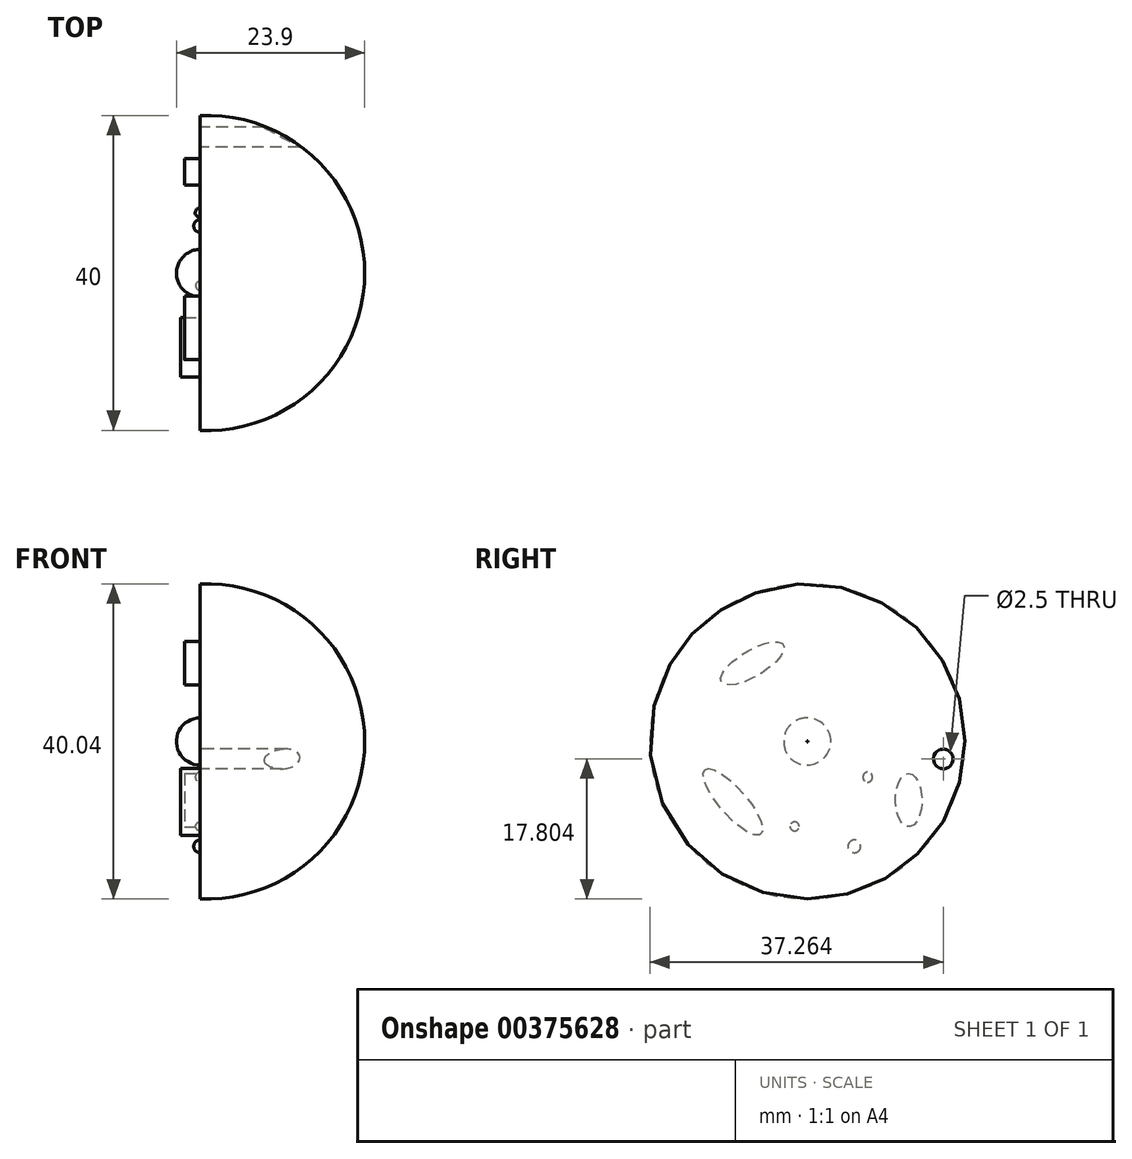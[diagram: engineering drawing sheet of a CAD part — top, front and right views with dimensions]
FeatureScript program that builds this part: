
annotation { "Feature Type Name" : "Feature", "Feature Type Description" : "" }
export const myFeature = defineFeature(function(context is Context, id is Id, definition is map)
    precondition{}
    {
        {
            var Q0;
            Q0=qCreatedBy(makeId("Front.planeOp"),FACE);
            var sketch = newSketch(context, id + "F0", { "sketchPlane" : qUnion([Q0])});
            skLineSegment(sketch, "E0", {"start": v(0, 0) * mm, "end": v(0, 20) * mm});
            skLineSegment(sketch, "E1", {"start": v(0, 0) * mm, "end": v(20.9, 0) * mm});
            skArc(sketch, "E2", {"start": v(20.9, 0) * mm, "mid": v(14.71, 14.46) * mm, "end": v(0, 20) * mm});
            skSolve(sketch);
        }
        {
            var Q0;
            Q0=makeQuery(id+"F0.imprint","IMPRINT",FACE,{"disambiguationData":[TD([[makeQuery(id+"F0.imprint","IMPRINT",EDGE,{"derivedFrom":sQuery(id+"F0.wireOp",EDGE,"E0")}),-1.0]])]});
            var Q1;
            Q1=sQuery(id+"F0.wireOp",EDGE,"E1");
            revolve(context, id + "F1", {"entities" : qUnion([Q0]), "axis" : qUnion([Q1]), "revolveType" : RevolveType.FULL});
        }
        {
            var Q0;
            Q0=qCreatedBy(makeId("Right.planeOp"),FACE);
            var sketch = newSketch(context, id + "F2", { "sketchPlane" : qUnion([Q0])});
            skLineSegment(sketch, "E3", {"start": v(0, 0) * mm, "end": v(0, 3) * mm});
            skLineSegment(sketch, "E4", {"start": v(0, 0) * mm, "end": v(-3, 0) * mm});
            skArc(sketch, "E5", {"start": v(0, 3) * mm, "mid": v(-2.14, 2.14) * mm, "end": v(-3, 0) * mm});
            skSolve(sketch);
        }
        {
            var Q0;
            Q0=qSketchRegion(id+"F2",true);
            var Q1;
            Q1=sQuery(id+"F2.wireOp",EDGE,"E4");
            revolve(context, id + "F3", {"operationType" : NewBodyOperationType.ADD, "entities" : qUnion([Q0]), "axis" : qUnion([Q1]), "revolveType" : RevolveType.FULL});
        }
        {
            var Q0;
            Q0=makeQuery(id+"F1.opRevolve","SWEPT_FACE",FACE,{"disambiguationData":[OSD([sQuery(id+"F0.wireOp",EDGE,"E0")])]});
            var sketch = newSketch(context, id + "F4", { "sketchPlane" : qUnion([Q0])});
            skLineSegment(sketch, "E6", {"start": v(0, 0) * mm, "end": v(-3, 0) * mm});
            skLineSegment(sketch, "E7", {"start": v(0, 0) * mm, "end": v(0, 3) * mm});
            skArc(sketch, "E8", {"start": v(0, 3) * mm, "mid": v(-2.1, 2.1) * mm, "end": v(-3, 0) * mm});
            skSolve(sketch);
        }
        {
            var Q0;
            Q0=makeQuery(id+"F4.imprint","IMPRINT",FACE,{"disambiguationData":[TD([[makeQuery(id+"F4.imprint","IMPRINT",EDGE,{"derivedFrom":sQuery(id+"F4.wireOp",EDGE,"E6")}),-1.0]])]});
            var Q1;
            Q1=sQuery(id+"F4.wireOp",EDGE,"E6");
            revolve(context, id + "F5", {"operationType" : NewBodyOperationType.ADD, "entities" : qUnion([Q0]), "axis" : qUnion([Q1]), "revolveType" : RevolveType.FULL});
        }
        {
            var Q0;
            Q0=makeQuery(id+"F1.opRevolve","SWEPT_FACE",FACE,{"disambiguationData":[OSD([sQuery(id+"F0.wireOp",EDGE,"E0")])]});
            var sketch = newSketch(context, id + "F6", { "sketchPlane" : qUnion([Q0])});
            skEllipse(sketch, "E9", {"center": v(9.46, -7.67) * mm, "majorRadius": 5.42 * mm, "minorRadius": 1.7 * mm, "majorAxis": v(0.66, 0.75)});
            skSolve(sketch);
        }
        {
            var Q0;
            Q0=qSketchRegion(id+"F6",true);
            extrude(context, id + "F7", {"entities" : qUnion([Q0]), "depth" : 2.5 * mm});
        }
        {
            var Q0;
            Q0=makeQuery(id+"F7.opExtrude","CAP_FACE",FACE,{"disambiguationData":[OSD([sQuery(id+"F6.wireOp",EDGE,"E9")])],"isStart":false});
            var sketch = newSketch(context, id + "F8", { "sketchPlane" : qUnion([Q0])});
            skFitSpline(sketch, "E10", {"points": [v(7.97, -11.28) * mm, v(6.8, -8.9) * mm, v(9.38, -10.19) * mm, v(8.17, -7.24) * mm, v(11, -8.49) * mm, v(9.27, -5.4) * mm, v(11.92, -6.7) * mm, v(11.05, -4) * mm, v(13.1, -5.01) * mm], "startDerivative": vector(-20.7, 30.85) * mm, "endDerivative": vector(27.66, -19.9) * mm});
            skSolve(sketch);
        }
        {
            var Q0;
            Q0=qSketchRegion(id+"F8",true);
            var Q1;
            Q1=sQuery(id+"F8.wireOp",EDGE,"E10");
            extrude(context, id + "F9", {"entities" : qUnion([Q0]), "bodyType" : ToolBodyType.SURFACE, "surfaceEntities" : qUnion([Q1]), "oppositeDirection" : true, "depth" : 2 * mm});
        }
        {
            var Q0;
            Q0=makeQuery(id+"F1.opRevolve","SWEPT_FACE",FACE,{"disambiguationData":[OSD([sQuery(id+"F0.wireOp",EDGE,"E0")])]});
            var sketch = newSketch(context, id + "F10", { "sketchPlane" : qUnion([Q0])});
            skSolve(sketch);
        }
        {
            var Q0;
            {var subQ1=sQuery(id+"F0.wireOp",EDGE,"E0");Q0=makeQuery(id+"F10.imprint","IMPRINT",FACE,{"disambiguationData":[TD([[makeQuery(id+"F10.imprint","IMPRINT",EDGE,{"derivedFrom":makeQuery(id+"F1.opRevolve","SWEPT_EDGE",EDGE,{"disambiguationData":[OSD([subQ1,sQuery(id+"F0.wireOp",EDGE,"E2")])]})}),1.0]])]});}
            var sketch = newSketch(context, id + "F11", { "sketchPlane" : qUnion([Q0])});
            skSolve(sketch);
        }
        {
            var Q0;
            {var subQ1=sQuery(id+"F0.wireOp",EDGE,"E0");Q0=makeQuery(id+"F10.imprint","IMPRINT",FACE,{"disambiguationData":[TD([[makeQuery(id+"F10.imprint","IMPRINT",EDGE,{"derivedFrom":makeQuery(id+"F1.opRevolve","SWEPT_EDGE",EDGE,{"disambiguationData":[OSD([subQ1,sQuery(id+"F0.wireOp",EDGE,"E2")])]})}),1.0]])]});}
            var sketch = newSketch(context, id + "F12", { "sketchPlane" : qUnion([Q0])});
            skEllipse(sketch, "E11", {"center": v(6.98, 9.93) * mm, "majorRadius": 4.6 * mm, "minorRadius": 1.66 * mm, "majorAxis": v(0.86, -0.51)});
            skSolve(sketch);
        }
        {
            var Q0;
            Q0=qSketchRegion(id+"F12",true);
            extrude(context, id + "F13", {"entities" : qUnion([Q0]), "depth" : 2 * mm});
        }
        {
            var Q0;
            Q0=makeQuery(id+"F13.opExtrude","CAP_FACE",FACE,{"disambiguationData":[OSD([sQuery(id+"F12.wireOp",EDGE,"E11")])],"isStart":false});
            var sketch = newSketch(context, id + "F14", { "sketchPlane" : qUnion([Q0])});
            skFitSpline(sketch, "E12", {"points": [v(4.68, 12.63) * mm, v(3.63, 10.54) * mm, v(6.2, 12.18) * mm, v(5.11, 9.18) * mm, v(7.84, 11.35) * mm, v(6.92, 8.06) * mm, v(9.45, 10.2) * mm, v(9.08, 7.26) * mm], "startDerivative": vector(-17.32, -26.87) * mm, "endDerivative": vector(-10.03, -33.63) * mm});
            skSolve(sketch);
        }
        {
            var Q0;
            Q0=qSketchRegion(id+"F14",true);
            var Q1;
            Q1=sQuery(id+"F14.wireOp",EDGE,"E12");
            extrude(context, id + "F15", {"entities" : qUnion([Q0]), "bodyType" : ToolBodyType.SURFACE, "surfaceEntities" : qUnion([Q1]), "oppositeDirection" : true, "depth" : 2 * mm});
        }
        {
            var Q0;
            {var subQ1=sQuery(id+"F0.wireOp",EDGE,"E0");Q0=makeQuery(id+"F10.imprint","IMPRINT",FACE,{"disambiguationData":[TD([[makeQuery(id+"F10.imprint","IMPRINT",EDGE,{"derivedFrom":makeQuery(id+"F1.opRevolve","SWEPT_EDGE",EDGE,{"disambiguationData":[OSD([subQ1,sQuery(id+"F0.wireOp",EDGE,"E2")])]})}),1.0]])]});}
            var sketch = newSketch(context, id + "F16", { "sketchPlane" : qUnion([Q0])});
            skFitSpline(sketch, "E13", {"points": [v(-13.4, 3.83) * mm, v(-13, 6.76) * mm, v(-11.02, 11.05) * mm, v(-7.06, 13.56) * mm, v(-3.83, 13.87) * mm, v(-2.72, 12.84) * mm, v(-4.78, 12.22) * mm, v(-7.76, 11.16) * mm, v(-9.8, 9.35) * mm, v(-10.94, 6.79) * mm, v(-11.41, 3.75) * mm, v(-10.83, 2.72) * mm, v(-9.4, 6.15) * mm, v(-7.32, 9.32) * mm, v(-3.78, 10.86) * mm, v(-3.25, 8.93) * mm, v(-5.3, 8.35) * mm, v(-7.26, 6.9) * mm, v(-8.35, 4.25) * mm, v(-7.57, 3.02) * mm, v(-6.48, 4.95) * mm, v(-5.4, 6.65) * mm, v(-2.94, 7.46) * mm, v(-2.5, 6.23) * mm, v(-4.8, 5.59) * mm, v(-6.14, 2.41) * mm], "startDerivative": vector(4.96, 65.1) * mm, "endDerivative": vector(-14.45, -88.75) * mm});
            skSolve(sketch);
        }
        {
            var Q0;
            Q0=qSketchRegion(id+"F16",true);
            var Q1;
            Q1=sQuery(id+"F16.wireOp",EDGE,"E13");
            extrude(context, id + "F17", {"entities" : qUnion([Q0]), "bodyType" : ToolBodyType.SURFACE, "surfaceEntities" : qUnion([Q1]), "depth" : 2 * mm});
        }
        {
            var Q0;
            {var subQ1=sQuery(id+"F0.wireOp",EDGE,"E0");Q0=makeQuery(id+"F10.imprint","IMPRINT",FACE,{"disambiguationData":[TD([[makeQuery(id+"F10.imprint","IMPRINT",EDGE,{"derivedFrom":makeQuery(id+"F1.opRevolve","SWEPT_EDGE",EDGE,{"disambiguationData":[OSD([subQ1,sQuery(id+"F0.wireOp",EDGE,"E2")])]})}),1.0]])]});}
            var sketch = newSketch(context, id + "F18", { "sketchPlane" : qUnion([Q0])});
            skFitSpline(sketch, "E14", {"points": [v(1.63, 7.11) * mm, v(4.78, 6.86) * mm, v(8.1, 5.2) * mm, v(9.66, 1.11) * mm, v(8.41, -3.01) * mm, v(4.67, -6.66) * mm, v(1.55, -7.21) * mm, v(1.07, -5.9) * mm, v(5.1, -4.45) * mm, v(7.63, -0.85) * mm, v(7.17, 3.33) * mm, v(4.59, 5.28) * mm, v(0, 5.94) * mm, v(0, 5.08) * mm, v(3.24, 4.42) * mm, v(5.82, 2.74) * mm, v(6.18, 0) * mm, v(5.56, -2.02) * mm, v(3.12, -3.79) * mm, v(1.15, -4.12) * mm, v(1.1, -3.42) * mm, v(3.12, -2.7) * mm, v(4.9, -0.76) * mm, v(4.7, 2.17) * mm, v(3.65, 3.54) * mm, v(1.42, 3.89) * mm, v(0, 3.94) * mm, v(0, 3.36) * mm, v(2.32, 3.19) * mm, v(3.68, 1.68) * mm, v(3.9, 0) * mm, v(3.27, -1.54) * mm, v(2.16, -2.36) * mm], "startDerivative": vector(88.94, -1.16) * mm, "endDerivative": vector(-52.62, -29.6) * mm});
            skSolve(sketch);
        }
        {
            var Q0;
            Q0=qSketchRegion(id+"F18",true);
            var Q1;
            Q1=sQuery(id+"F18.wireOp",EDGE,"E14");
            extrude(context, id + "F19", {"entities" : qUnion([Q0]), "bodyType" : ToolBodyType.SURFACE, "surfaceEntities" : qUnion([Q1]), "depth" : 1.8 * mm});
        }
        {
            var Q0;
            {var subQ1=sQuery(id+"F0.wireOp",EDGE,"E0");Q0=makeQuery(id+"F10.imprint","IMPRINT",FACE,{"disambiguationData":[TD([[makeQuery(id+"F10.imprint","IMPRINT",EDGE,{"derivedFrom":makeQuery(id+"F1.opRevolve","SWEPT_EDGE",EDGE,{"disambiguationData":[OSD([subQ1,sQuery(id+"F0.wireOp",EDGE,"E2")])]})}),1.0]])]});}
            var sketch = newSketch(context, id + "F20", { "sketchPlane" : qUnion([Q0])});
            skLineSegment(sketch, "E15", {"start": v(-7.66, -5.18) * mm, "end": v(-7.66, -3.88) * mm});
            skArc(sketch, "E16", {"start": v(-7.66, -3.88) * mm, "mid": v(-8.27, -4.53) * mm, "end": v(-7.66, -5.18) * mm});
            skSolve(sketch);
        }
        {
            var Q0;
            Q0=qSketchRegion(id+"F20",true);
            var Q1;
            Q1=sQuery(id+"F20.wireOp",EDGE,"E15");
            revolve(context, id + "F21", {"operationType" : NewBodyOperationType.ADD, "entities" : qUnion([Q0]), "axis" : qUnion([Q1]), "revolveType" : RevolveType.FULL});
        }
        {
            var Q0;
            {var subQ1=sQuery(id+"F0.wireOp",EDGE,"E0");Q0=makeQuery(id+"F10.imprint","IMPRINT",FACE,{"disambiguationData":[TD([[makeQuery(id+"F10.imprint","IMPRINT",EDGE,{"derivedFrom":makeQuery(id+"F1.opRevolve","SWEPT_EDGE",EDGE,{"disambiguationData":[OSD([subQ1,sQuery(id+"F0.wireOp",EDGE,"E2")])]})}),1.0]])]});}
            var sketch = newSketch(context, id + "F22", { "sketchPlane" : qUnion([Q0])});
            skLineSegment(sketch, "E17", {"start": v(-5.97, -14.13) * mm, "end": v(-5.97, -12.52) * mm});
            skArc(sketch, "E18", {"start": v(-5.97, -12.52) * mm, "mid": v(-6.78, -13.33) * mm, "end": v(-5.97, -14.13) * mm});
            skSolve(sketch);
        }
        {
            var Q0;
            Q0=qSketchRegion(id+"F22",true);
            var Q1;
            Q1=sQuery(id+"F22.wireOp",EDGE,"E17");
            revolve(context, id + "F23", {"operationType" : NewBodyOperationType.ADD, "entities" : qUnion([Q0]), "axis" : qUnion([Q1]), "revolveType" : RevolveType.FULL});
        }
        {
            var Q0;
            {var subQ1=sQuery(id+"F0.wireOp",EDGE,"E0");Q0=makeQuery(id+"F11.imprint","IMPRINT",FACE,{"disambiguationData":[TD([[makeQuery(id+"F11.imprint","IMPRINT",EDGE,{"derivedFrom":makeQuery(id+"F10.imprint","IMPRINT",EDGE,{"derivedFrom":makeQuery(id+"F1.opRevolve","SWEPT_EDGE",EDGE,{"disambiguationData":[OSD([subQ1,sQuery(id+"F0.wireOp",EDGE,"E2")])]})})}),1.0]])]});}
            var sketch = newSketch(context, id + "F24", { "sketchPlane" : qUnion([Q0])});
            skEllipse(sketch, "E19", {"center": v(-12.87, -7.45) * mm, "majorRadius": 3.4 * mm, "minorRadius": 1.69 * mm, "majorAxis": v(0, 1)});
            skSolve(sketch);
        }
        {
            var Q0;
            Q0=qSketchRegion(id+"F24",true);
            extrude(context, id + "F25", {"entities" : qUnion([Q0]), "depth" : 2 * mm});
        }
        {
            var Q0;
            Q0=makeQuery(id+"F25.opExtrude","CAP_FACE",FACE,{"disambiguationData":[OSD([sQuery(id+"F24.wireOp",EDGE,"E19")])],"isStart":false});
            var sketch = newSketch(context, id + "F26", { "sketchPlane" : qUnion([Q0])});
            skFitSpline(sketch, "E20", {"points": [v(-11.66, -9.82) * mm, v(-14.04, -9.89) * mm, v(-11.29, -8.66) * mm, v(-14.53, -7.96) * mm, v(-11.19, -7.13) * mm, v(-14.5, -6.55) * mm, v(-11.4, -5.75) * mm, v(-14.12, -5.2) * mm], "startDerivative": vector(-32.3, -3.08) * mm, "endDerivative": vector(-34.6, 3.54) * mm});
            skSolve(sketch);
        }
        {
            var Q0;
            Q0=qSketchRegion(id+"F26",true);
            var Q1;
            Q1=sQuery(id+"F26.wireOp",EDGE,"E20");
            extrude(context, id + "F27", {"entities" : qUnion([Q0]), "bodyType" : ToolBodyType.SURFACE, "surfaceEntities" : qUnion([Q1]), "oppositeDirection" : true, "depth" : 2 * mm});
        }
        {
            var Q0;
            {var subQ1=sQuery(id+"F0.wireOp",EDGE,"E0");Q0=makeQuery(id+"F11.imprint","IMPRINT",FACE,{"disambiguationData":[TD([[makeQuery(id+"F11.imprint","IMPRINT",EDGE,{"derivedFrom":makeQuery(id+"F10.imprint","IMPRINT",EDGE,{"derivedFrom":makeQuery(id+"F1.opRevolve","SWEPT_EDGE",EDGE,{"disambiguationData":[OSD([subQ1,sQuery(id+"F0.wireOp",EDGE,"E2")])]})})}),1.0]])]});}
            var sketch = newSketch(context, id + "F28", { "sketchPlane" : qUnion([Q0])});
            skLineSegment(sketch, "E21", {"start": v(1.04, -10.79) * mm, "end": v(2.2, -10.79) * mm});
            skArc(sketch, "E22", {"start": v(2.2, -10.79) * mm, "mid": v(1.62, -10.22) * mm, "end": v(1.04, -10.79) * mm});
            skSolve(sketch);
        }
        {
            var Q0;
            Q0=qSketchRegion(id+"F28",true);
            var Q1;
            Q1=sQuery(id+"F28.wireOp",EDGE,"E21");
            revolve(context, id + "F29", {"operationType" : NewBodyOperationType.ADD, "entities" : qUnion([Q0]), "axis" : qUnion([Q1]), "revolveType" : RevolveType.FULL});
        }
        {
            var Q0;
            {var subQ1=sQuery(id+"F0.wireOp",EDGE,"E0");Q0=makeQuery(id+"F11.imprint","IMPRINT",FACE,{"disambiguationData":[TD([[makeQuery(id+"F11.imprint","IMPRINT",EDGE,{"derivedFrom":makeQuery(id+"F10.imprint","IMPRINT",EDGE,{"derivedFrom":makeQuery(id+"F1.opRevolve","SWEPT_EDGE",EDGE,{"disambiguationData":[OSD([subQ1,sQuery(id+"F0.wireOp",EDGE,"E2")])]})})}),1.0]])]});}
            var sketch = newSketch(context, id + "F30", { "sketchPlane" : qUnion([Q0])});
            skCircle(sketch, "E23", {"center": v(2.2, -18.68) * mm, "radius": 0.6 * mm});
            skPoint(sketch, "E23.first.point", {"position": v(2.5, -18.15) * mm});
            skPoint(sketch, "E23.second.point", {"position": v(2.25, -19.28) * mm});
            skPoint(sketch, "E23.third.point", {"position": v(1.71, -18.3) * mm});
            skSolve(sketch);
        }
        {
            var Q0;
            Q0=qSketchRegion(id+"F30",true);
            extrude(context, id + "F31", {"entities" : qUnion([Q0]), "operationType" : NewBodyOperationType.REMOVE, "depth" : 20 * mm});
        }
        {
            var Q0;
            Q0=makeQuery(id+"F1.opRevolve","SWEPT_FACE",FACE,{"disambiguationData":[OSD([sQuery(id+"F0.wireOp",EDGE,"E0")])]});
            var sketch = newSketch(context, id + "F32", { "sketchPlane" : qUnion([Q0])});
            skCircle(sketch, "E24", {"center": v(-17.26, -2.22) * mm, "radius": 1.25 * mm});
            skSolve(sketch);
        }
        {
            var Q0;
            Q0 = qSketchRegion(id + "F32", true);
            extrude(context, id + "F33", {"entities" : qUnion([Q0]), "operationType" : NewBodyOperationType.REMOVE, "oppositeDirection" : true, "depth" : 25 * mm});
        }
    });
